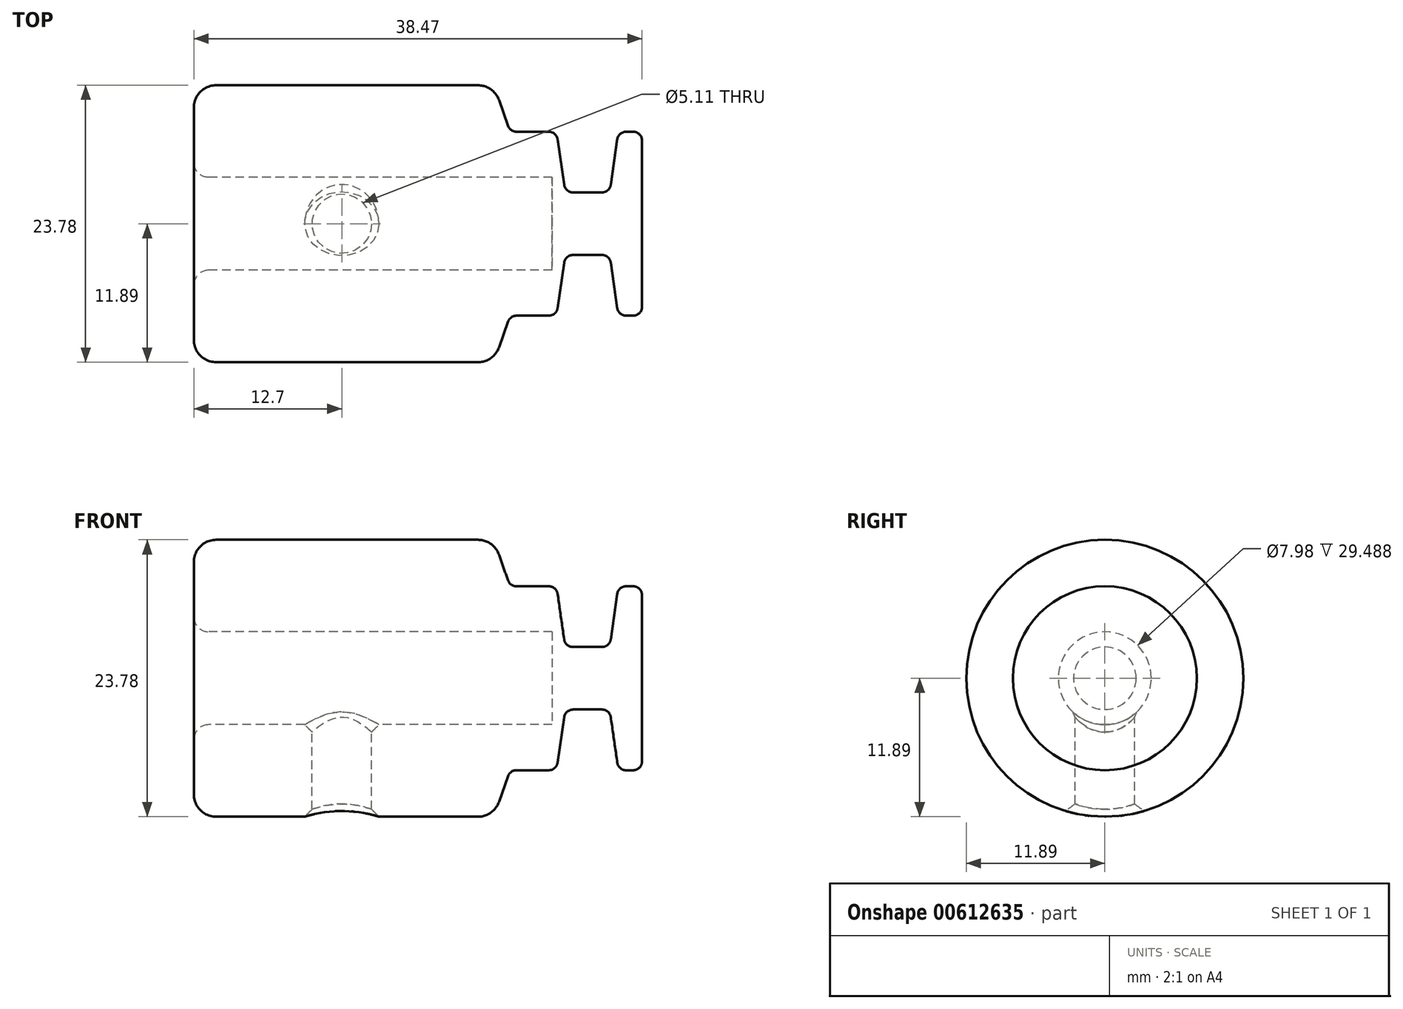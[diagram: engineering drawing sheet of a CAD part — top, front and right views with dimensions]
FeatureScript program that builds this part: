
annotation { "Feature Type Name" : "Feature", "Feature Type Description" : "" }
export const myFeature = defineFeature(function(context is Context, id is Id, definition is map)
    precondition{}
    {
        {
            var Q0;
            Q0=qCreatedBy(makeId("Top.planeOp"),FACE);
            var sketch = newSketch(context, id + "F0", { "sketchPlane" : qUnion([Q0])});
            skLineSegment(sketch, "E0", {"start": v(-39.61, 0) * mm, "end": v(40.88, 0) * mm});
            skLineSegment(sketch, "E1", {"start": v(-11.43, 3.99) * mm, "end": v(18.06, 3.99) * mm});
            skLineSegment(sketch, "E2", {"start": v(31.41, 7.9) * mm, "end": v(31.41, 11.27) * mm});
            skLineSegment(sketch, "E3", {"start": v(15.69, 15.88) * mm, "end": v(11.64, 15.88) * mm});
            skPoint(sketch, "E4.startSnap0", {"position": v(-21.2, 9.35) * mm});
            skLineSegment(sketch, "E5", {"start": v(-12.7, 11.89) * mm, "end": v(-12.7, 5.26) * mm});
            skPoint(sketch, "E6.visualSharp", {"position": v(-12.7, 15.88) * mm});
            skArc(sketch, "E6.filletArc", {"start": v(-12.07, 15.88) * mm, "mid": v(-12.51, 15.69) * mm, "end": v(-12.7, 15.24) * mm});
            skArc(sketch, "E7.filletArc", {"start": v(-12.7, 5.26) * mm, "mid": v(-12.33, 4.36) * mm, "end": v(-11.43, 3.99) * mm});
            skPoint(sketch, "E8.visualSharp", {"position": v(31.41, 3.99) * mm});
            skPoint(sketch, "E9.visualSharp", {"position": v(31.41, 15.88) * mm});
            skPoint(sketch, "E10.visualSharp", {"position": v(23.2, 11.3) * mm});
            skPoint(sketch, "E11.visualSharp", {"position": v(19.8, -6.08) * mm});
            skPoint(sketch, "E12", {"position": v(0, 15.88) * mm});
            skPoint(sketch, "E13.visualSharp", {"position": v(25.82, 14.6) * mm});
            skPoint(sketch, "E14.visualSharp", {"position": v(17.27, 15.88) * mm});
            skLineSegment(sketch, "E15", {"start": v(21.08, 3.99) * mm, "end": v(23.17, 3.99) * mm});
            skLineSegment(sketch, "E16", {"start": v(31.41, 11.27) * mm, "end": v(31.41, 4.73) * mm});
            skLineSegment(sketch, "E17", {"start": v(31.41, 7.9) * mm, "end": v(31.41, 15.23) * mm});
            skArc(sketch, "E18.filletArc", {"start": v(30.67, 3.99) * mm, "mid": v(31.2, 4.2) * mm, "end": v(31.41, 4.73) * mm});
            skPoint(sketch, "E19.end.orphan", {"position": v(27.74, 14.69) * mm});
            skPoint(sketch, "E13.filletArc.start.orphan", {"position": v(26.12, 14.69) * mm});
            skPoint(sketch, "E20.visualSharp", {"position": v(24.9, 15.88) * mm});
            skPoint(sketch, "E21.filletArc.end.orphan", {"position": v(29.04, 15.88) * mm});
            skLineSegment(sketch, "E22", {"start": v(15.69, 15.88) * mm, "end": v(31.41, 15.88) * mm});
            skLineSegment(sketch, "E23", {"start": v(31.41, 15.88) * mm, "end": v(31.41, 15.23) * mm});
            skLineSegment(sketch, "E24", {"start": v(5.98, -3.53) * mm, "end": v(5.98, -4.45) * mm});
            skLineSegment(sketch, "E25", {"start": v(21.08, 2.69) * mm, "end": v(21.08, 15.88) * mm});
            skLineSegment(sketch, "E26", {"start": v(17.27, 15.88) * mm, "end": v(19.18, 2.69) * mm});
            skLineSegment(sketch, "E27", {"start": v(24.9, 15.88) * mm, "end": v(22.99, 2.69) * mm});
            skCircle(sketch, "E28", {"center": v(21.08, 7.62) * mm, "radius": 2.45 * mm});
            skLineSegment(sketch, "E29", {"start": v(23.74, 7.9) * mm, "end": v(31.41, 7.9) * mm});
            skLineSegment(sketch, "E30", {"start": v(18.42, 7.9) * mm, "end": v(14.44, 7.9) * mm});
            skLineSegment(sketch, "E31", {"start": v(14.44, 7.9) * mm, "end": v(13.04, 11.89) * mm});
            skLineSegment(sketch, "E32", {"start": v(18.06, 3.99) * mm, "end": v(18.06, 0) * mm});
            skLineSegment(sketch, "E33", {"start": v(18.06, 0) * mm, "end": v(27.3, 0) * mm});
            skLineSegment(sketch, "E34.trimOffspring", {"start": v(18.99, 3.99) * mm, "end": v(21.08, 3.99) * mm});
            skLineSegment(sketch, "E35.trimOffspring", {"start": v(27.3, 3.99) * mm, "end": v(30.67, 3.99) * mm});
            skLineSegment(sketch, "E36", {"start": v(19.18, 2.69) * mm, "end": v(22.99, 2.69) * mm});
            skPoint(sketch, "E37.orphan", {"position": v(19.27, 2.04) * mm});
            skPoint(sketch, "E38.orphan", {"position": v(22.8, 1.45) * mm});
            skPoint(sketch, "E39.orphan", {"position": v(21.08, 1.45) * mm});
            skLineSegment(sketch, "E40", {"start": v(25.77, 7.9) * mm, "end": v(25.77, 0) * mm});
            skLineSegment(sketch, "E41", {"start": v(13.04, 11.89) * mm, "end": v(-12.7, 11.89) * mm});
            skSolve(sketch);
        }
        {
            var Q0;
            Q0=makeQuery(id+"F0.imprint","IMPRINT",FACE,{"disambiguationData":[TD([[makeQuery(id+"F0.imprint","IMPRINT",EDGE,{"derivedFrom":sQuery(id+"F0.wireOp",EDGE,"E1")}),1.0]])]});
            var Q1;
            Q1=sQuery(id+"F0.wireOp",EDGE,"E0");
            revolve(context, id + "F1", {"surfaceOperationType" : NewSurfaceOperationType.NEW, "entities" : qUnion([Q0]), "axis" : qUnion([Q1]), "revolveType" : RevolveType.FULL});
        }
        {
            var Q0;
            Q0=qCreatedBy(makeId("Top.planeOp"),FACE);
            var sketch = newSketch(context, id + "F2", { "sketchPlane" : qUnion([Q0])});
            skCircle(sketch, "E42", {"center": v(0, 0) * mm, "radius": 2.55 * mm});
            skSolve(sketch);
        }
        {
            var Q0;
            Q0=qSketchRegion(id+"F2",true);
            extrude(context, id + "F3", {"entities" : qUnion([Q0]), "operationType" : NewBodyOperationType.REMOVE, "oppositeDirection" : true, "depth" : 25.4 * mm, "offsetDistance" : 25.4 * mm});
        }
        {
            var Q0;
            Q0=makeQuery(id+"F1.opRevolve","SWEPT_EDGE",EDGE,{"disambiguationData":[OSD([sQuery(id+"F0.wireOp",EDGE,"E5"),sQuery(id+"F0.wireOp",EDGE,"E41")])]});
            var Q1;
            Q1=makeQuery(id+"F1.opRevolve","SWEPT_EDGE",EDGE,{"disambiguationData":[OSD([sQuery(id+"F0.wireOp",EDGE,"E31"),sQuery(id+"F0.wireOp",EDGE,"E41")])]});
            fillet(context, id + "F4", {"entities" : qUnion([Q0, Q1]), "radius" : 1.9 * mm, "tangentPropagation" : true, "allowEdgeOverflow" : false});
        }
        {
            var Q0;
            Q0=makeQuery(id+"F1.opRevolve","SWEPT_EDGE",EDGE,{"disambiguationData":[OSD([sQuery(id+"F0.wireOp",EDGE,"E29"),sQuery(id+"F0.wireOp",EDGE,"atygfXIt-PjWA-5cL2-H3L0-17obKzaYe3I0")])]});
            var Q1;
            Q1=makeQuery(id+"F1.opRevolve","SWEPT_EDGE",EDGE,{"disambiguationData":[OSD([sQuery(id+"F0.wireOp",EDGE,"E26"),sQuery(id+"F0.wireOp",EDGE,"E30")])]});
            var Q2;
            Q2=makeQuery(id+"F1.opRevolve","SWEPT_EDGE",EDGE,{"disambiguationData":[OSD([sQuery(id+"F0.wireOp",EDGE,"E27"),sQuery(id+"F0.wireOp",EDGE,"E29")])]});
            var Q3;
            Q3=makeQuery(id+"F1.opRevolve","SWEPT_EDGE",EDGE,{"disambiguationData":[OSD([sQuery(id+"F0.wireOp",EDGE,"0rcbiWEG-W2dT-9Jic-OKi2-vRfkh0FIArc8"),sQuery(id+"F0.wireOp",EDGE,"E27")])]});
            var Q4;
            Q4=makeQuery(id+"F1.opRevolve","SWEPT_EDGE",EDGE,{"disambiguationData":[OSD([sQuery(id+"F0.wireOp",EDGE,"0rcbiWEG-W2dT-9Jic-OKi2-vRfkh0FIArc8"),sQuery(id+"F0.wireOp",EDGE,"E26")])]});
            var Q5;
            Q5=makeQuery(id+"F1.opRevolve","SWEPT_EDGE",EDGE,{"disambiguationData":[OSD([sQuery(id+"F0.wireOp",EDGE,"E30"),sQuery(id+"F0.wireOp",EDGE,"E31")])]});
            fillet(context, id + "F5", {"entities" : qUnion([Q0, Q1, Q2, Q3, Q4, Q5]), "radius" : 0.76 * mm, "tangentPropagation" : true, "allowEdgeOverflow" : false});
        }
        {
            var Q0;
            Q0=makeQuery(id+"F3.boolean.opBoolean","INTERSECT",EDGE,{"derivedFrom":[makeQuery(id+"F1.opRevolve","SWEPT_FACE",FACE,{"disambiguationData":[OSD([sQuery(id+"F0.wireOp",EDGE,"E41")])]}),makeQuery(id+"F3.opExtrude","SWEPT_FACE",FACE,{"disambiguationData":[OSD([sQuery(id+"F2.wireOp",EDGE,"E42")])]})]});
            var Q1;
            Q1=makeQuery(id+"F3.boolean.opBoolean","COPY",FACE,{"derivedFrom":makeQuery(id+"F3.opExtrude","SWEPT_FACE",FACE,{"disambiguationData":[OSD([sQuery(id+"F2.wireOp",EDGE,"E42")])]})});
            chamfer(context, id + "F6", {"entities" : qUnion([Q0, Q1]), "width" : 0.64 * mm, "tangentPropagation" : true});
        }
    });
